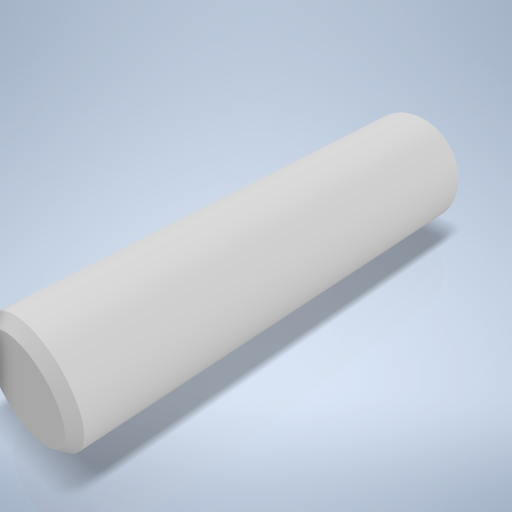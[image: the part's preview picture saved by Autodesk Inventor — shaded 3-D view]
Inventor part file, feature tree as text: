
AUTODESK INVENTOR PART (.ipt)
format: ipt  version: 2024.2 (Build 282272000, 272)  size: 231,424 bytes
history: native  units: mm
features: extrude x1, chamfer x1, sketch x1
ambient origin geometry x8: Origin, YZ Plane, XZ Plane, XY Plane, X Axis, Y Axis, Z Axis, Center Point
bodies: Volumenkörper1 (feature_tree)
feature tree (3):
  extrude  "Extrusion1"  Depth=10.0mm TaperAngle=0.0deg
  chamfer  "Fasen1"  Distance=0.2mm Angle=45.0deg
  sketch  "Skizze1"  dims[d0=2.5mm d1=10.0mm d2=0.0mm d3=0.2mm d4=2.0mm d5=45.0deg]
